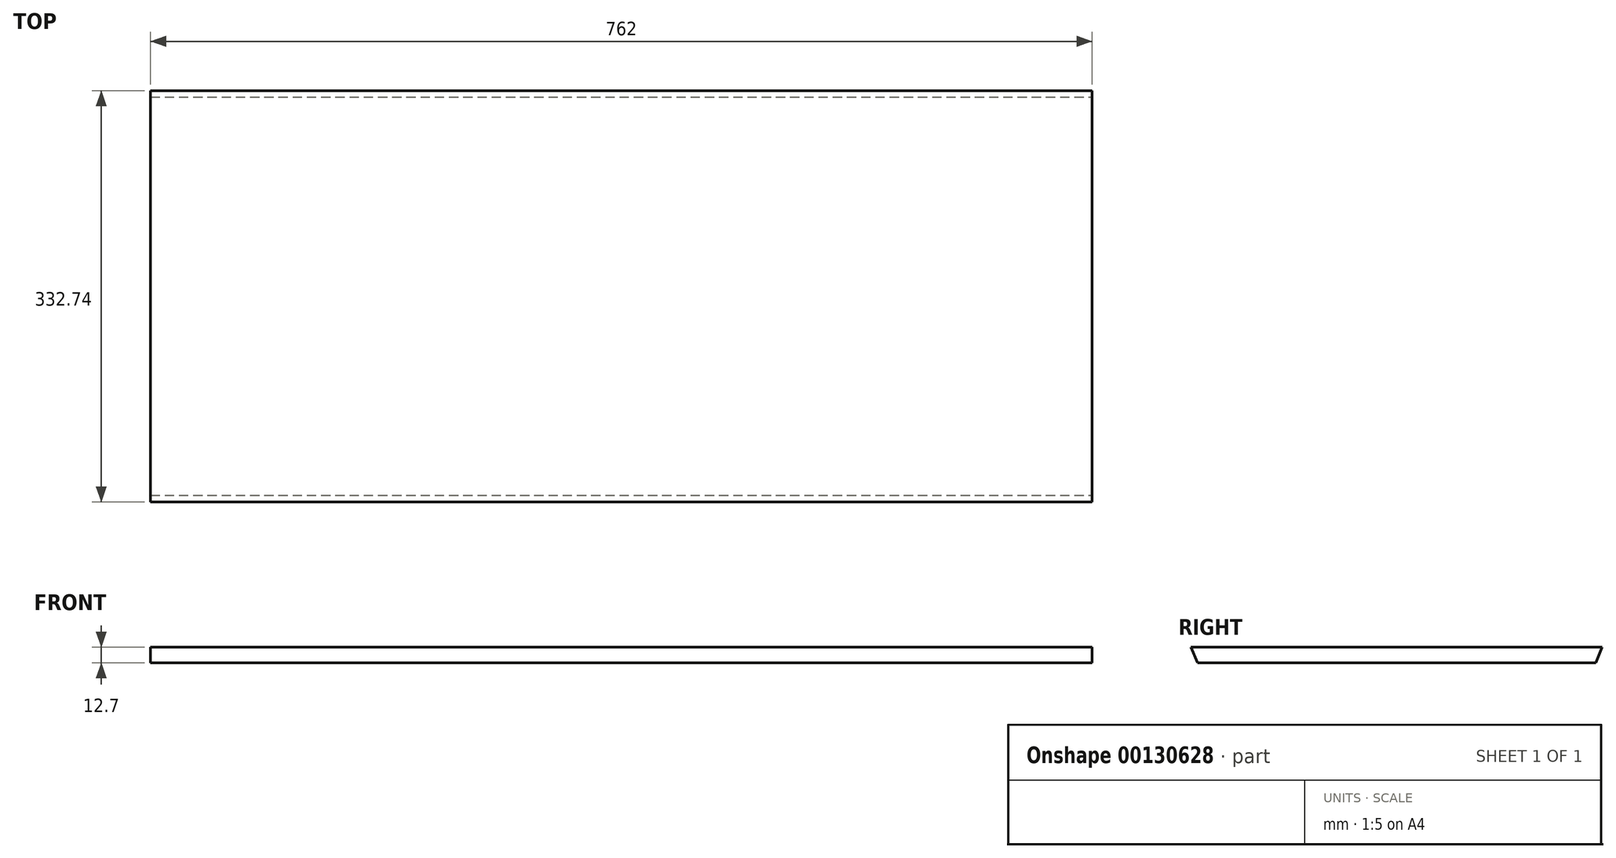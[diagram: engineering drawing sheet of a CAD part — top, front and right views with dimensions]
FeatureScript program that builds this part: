
annotation { "Feature Type Name" : "Feature", "Feature Type Description" : "" }
export const myFeature = defineFeature(function(context is Context, id is Id, definition is map)
    precondition{}
    {
        {
            var Q0;
            Q0=qCreatedBy(makeId("Top.planeOp"),FACE);
            var sketch = newSketch(context, id + "F0", { "sketchPlane" : qUnion([Q0])});
            skLineSegment(sketch, "E0.bottom", {"start": v(0, 0) * mm, "end": v(762, 0) * mm});
            skLineSegment(sketch, "E0.top", {"start": v(0, 322.22) * mm, "end": v(762, 322.22) * mm});
            skLineSegment(sketch, "E0.left", {"start": v(0, 0) * mm, "end": v(0, 322.22) * mm});
            skLineSegment(sketch, "E0.right", {"start": v(762, 0) * mm, "end": v(762, 322.22) * mm});
            skSolve(sketch);
        }
        {
            var Q0;
            Q0=makeQuery(id+"F0.imprint","IMPRINT",FACE,{"disambiguationData":[TD([[makeQuery(id+"F0.imprint","IMPRINT",EDGE,{"derivedFrom":sQuery(id+"F0.wireOp",EDGE,"E0.bottom")}),1.0]])]});
            extrude(context, id + "F1", {"entities" : qUnion([Q0]), "depth" : 12.7 * mm});
        }
        {
            var Q0;
            Q0=makeQuery(id+"F1.opExtrude","SWEPT_FACE",FACE,{"disambiguationData":[OSD([sQuery(id+"F0.wireOp",EDGE,"E0.right")])]});
            var sketch = newSketch(context, id + "F2", { "sketchPlane" : qUnion([Q0])});
            skLineSegment(sketch, "E1", {"start": v(0, 0) * mm, "end": v(0, 12.7) * mm});
            skLineSegment(sketch, "E2", {"start": v(0, 12.7) * mm, "end": v(-5.26, 12.7) * mm});
            skLineSegment(sketch, "E3", {"start": v(-5.26, 12.7) * mm, "end": v(0, 0) * mm});
            skLineSegment(sketch, "E4", {"start": v(322.22, 0) * mm, "end": v(322.22, 12.7) * mm});
            skLineSegment(sketch, "E5", {"start": v(322.22, 12.7) * mm, "end": v(327.48, 12.7) * mm});
            skLineSegment(sketch, "E6", {"start": v(327.48, 12.7) * mm, "end": v(322.22, 0) * mm});
            skSolve(sketch);
        }
        {
            var Q0;
            Q0=makeQuery(id+"F2.imprint","IMPRINT",FACE,{"disambiguationData":[TD([[makeQuery(id+"F2.imprint","IMPRINT",EDGE,{"derivedFrom":sQuery(id+"F2.wireOp",EDGE,"E1")}),-1.0]])]});
            var Q1;
            Q1=makeQuery(id+"F2.imprint","IMPRINT",FACE,{"disambiguationData":[TD([[makeQuery(id+"F2.imprint","IMPRINT",EDGE,{"derivedFrom":sQuery(id+"F2.wireOp",EDGE,"E4")}),1.0]])]});
            var Q2;
            Q2=makeQuery(id+"F1.opExtrude","SWEPT_FACE",FACE,{"disambiguationData":[OSD([sQuery(id+"F0.wireOp",EDGE,"E0.left")])]});
            extrude(context, id + "F3", {"entities" : qUnion([Q0, Q1]), "operationType" : NewBodyOperationType.ADD, "endBound" : BoundingType.UP_TO_SURFACE, "oppositeDirection" : true, "endBoundEntityFace" : qUnion([Q2]), "depth" : 25.4 * mm});
        }
    });
